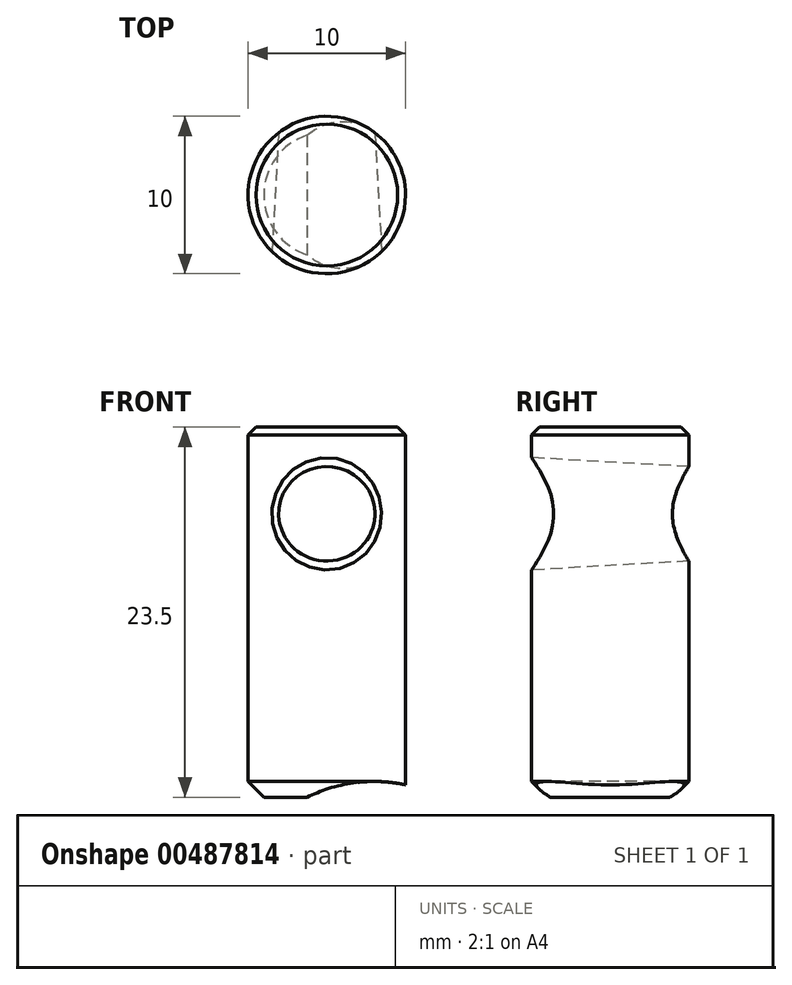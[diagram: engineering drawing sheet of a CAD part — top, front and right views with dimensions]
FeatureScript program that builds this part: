
annotation { "Feature Type Name" : "Feature", "Feature Type Description" : "" }
export const myFeature = defineFeature(function(context is Context, id is Id, definition is map)
    precondition{}
    {
        {
            var Q0;
            Q0=qCreatedBy(makeId("Top.planeOp"),FACE);
            var sketch = newSketch(context, id + "F0", { "sketchPlane" : qUnion([Q0])});
            skCircle(sketch, "E0", {"center": v(0, 0) * mm, "radius": 5 * mm});
            skSolve(sketch);
        }
        {
            var Q0;
            Q0=qCreatedBy(makeId("Front.planeOp"),FACE);
            var sketch = newSketch(context, id + "F1", { "sketchPlane" : qUnion([Q0])});
            skCircle(sketch, "E1", {"center": v(3, -9.5) * mm, "radius": 9.5 * mm});
            skSolve(sketch);
        }
        {
            var Q0;
            Q0 = qSketchRegion(id + "F0", true);
            extrude(context, id + "F2", {"entities" : qUnion([Q0]), "depth" : 22.5 * mm, "offsetDistance" : 25 * mm, "hasSecondDirection" : true, "secondDirectionOppositeDirection" : true, "secondDirectionDepth" : 1 * mm});
        }
        {
            var Q0;
            Q0 = qSketchRegion(id + "F1", true);
            extrude(context, id + "F3", {"entities" : qUnion([Q0]), "operationType" : NewBodyOperationType.REMOVE, "endBound" : BoundingType.THROUGH_ALL, "oppositeDirection" : true, "depth" : 25 * mm, "offsetDistance" : 25 * mm, "hasSecondDirection" : true, "secondDirectionOppositeDirection" : false, "secondDirectionDepth" : 25 * mm});
        }
        {
            var Q0;
            Q0=makeQuery(id+"F2.opExtrude","CAP_EDGE",EDGE,{"disambiguationData":[OSD([sQuery(id+"F0.wireOp",EDGE,"E0")])],"isStart":true});
            chamfer(context, id + "F4", {"entities" : qUnion([Q0]), "width" : 1 * mm, "tangentPropagation" : true});
        }
        {
            var Q0;
            Q0=qCreatedBy(makeId("Front.planeOp"),FACE);
            var sketch = newSketch(context, id + "F5", { "sketchPlane" : qUnion([Q0])});
            skCircle(sketch, "E2", {"center": v(0, 17) * mm, "radius": 3 * mm});
            skSolve(sketch);
        }
        {
            var Q0;
            Q0 = qSketchRegion(id + "F5", true);
            extrude(context, id + "F6", {"entities" : qUnion([Q0]), "operationType" : NewBodyOperationType.ADD, "endBound" : BoundingType.SYMMETRIC, "depth" : 10 * mm, "offsetDistance" : 25 * mm});
        }
        {
            var Q0;
            Q0=makeQuery(id+"F6.opExtrude","CAP_FACE",FACE,{"disambiguationData":[OSD([sQuery(id+"F5.wireOp",EDGE,"E2")])],"isStart":true});
            var sketch = newSketch(context, id + "F7", { "sketchPlane" : qUnion([Q0])});
            skCircle(sketch, "E3", {"center": v(0, 17) * mm, "radius": 3 * mm});
            skSolve(sketch);
        }
        {
            var Q0;
            Q0 = qSketchRegion(id + "F7", true);
            extrude(context, id + "F8", {"entities" : qUnion([Q0]), "operationType" : NewBodyOperationType.REMOVE, "oppositeDirection" : true, "depth" : 10 * mm, "offsetDistance" : 25 * mm, "hasDraft" : true, "draftAngle" : 3.25 * degree});
        }
        {
            var Q0;
            Q0=makeQuery(id+"F2.opExtrude","CAP_EDGE",EDGE,{"disambiguationData":[OSD([sQuery(id+"F0.wireOp",EDGE,"E0")])],"isStart":false});
            chamfer(context, id + "F9", {"entities" : qUnion([Q0]), "width" : .5 * mm, "tangentPropagation" : true});
        }
    });
